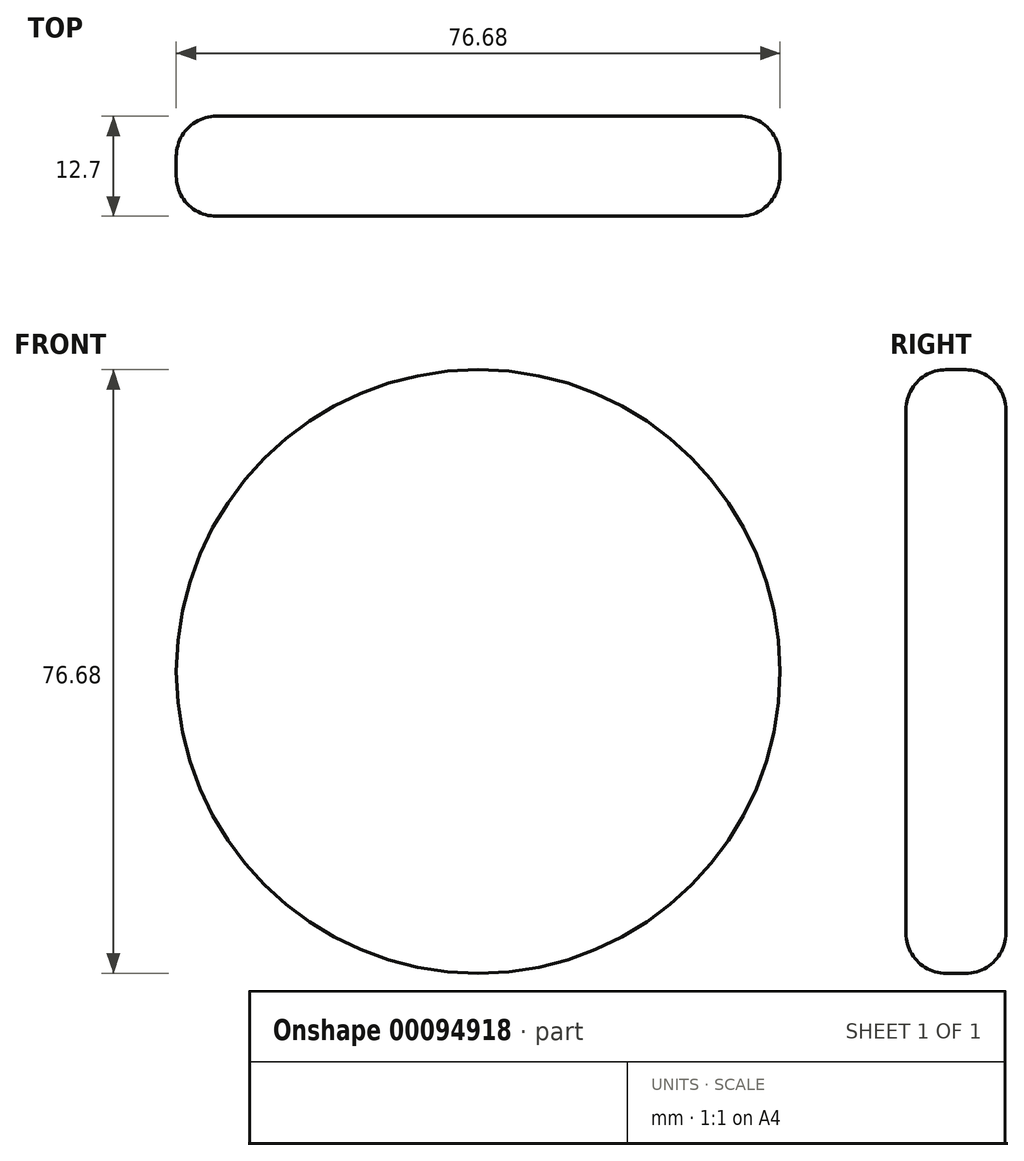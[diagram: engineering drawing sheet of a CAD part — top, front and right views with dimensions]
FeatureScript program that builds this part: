
annotation { "Feature Type Name" : "Feature", "Feature Type Description" : "" }
export const myFeature = defineFeature(function(context is Context, id is Id, definition is map)
    precondition{}
    {
        {
            var Q0;
            Q0=qCreatedBy(makeId("Front.planeOp"),FACE);
            var sketch = newSketch(context, id + "F0", { "sketchPlane" : qUnion([Q0])});
            skCircle(sketch, "E0", {"center": v(0, 0) * mm, "radius": 38.34 * mm});
            skSolve(sketch);
        }
        {
            var Q0;
            Q0=makeQuery(id+"F0.imprint","IMPRINT",FACE,{"disambiguationData":[TD([[makeQuery(id+"F0.imprint","IMPRINT",EDGE,{"derivedFrom":sQuery(id+"F0.wireOp",EDGE,"E0")}),1.0]])]});
            var sketch = newSketch(context, id + "F1", { "sketchPlane" : qUnion([Q0])});
            skSolve(sketch);
        }
        {
            var Q0;
            Q0 = qSketchRegion(id + "F1", true);
            var Q1;
            Q1=makeQuery(id+"F0.imprint","IMPRINT",FACE,{"disambiguationData":[TD([[makeQuery(id+"F0.imprint","IMPRINT",EDGE,{"derivedFrom":sQuery(id+"F0.wireOp",EDGE,"E0")}),1.0]])]});
            extrude(context, id + "F2", {"entities" : qUnion([Q0, Q1]), "depth" : 12.7 * mm});
        }
        {
            var Q0;
            Q0=makeQuery(id+"F2.opExtrude","CAP_EDGE",EDGE,{"disambiguationData":[OSD([sQuery(id+"F0.wireOp",EDGE,"E0")])],"isStart":false});
            var Q1;
            Q1=makeQuery(id+"F2.opExtrude","CAP_EDGE",EDGE,{"disambiguationData":[OSD([sQuery(id+"F0.wireOp",EDGE,"E0")])],"isStart":true});
            fillet(context, id + "F3", {"entities" : qUnion([Q0, Q1]), "radius" : 5.08 * mm, "tangentPropagation" : true, "allowEdgeOverflow" : false});
        }
    });
